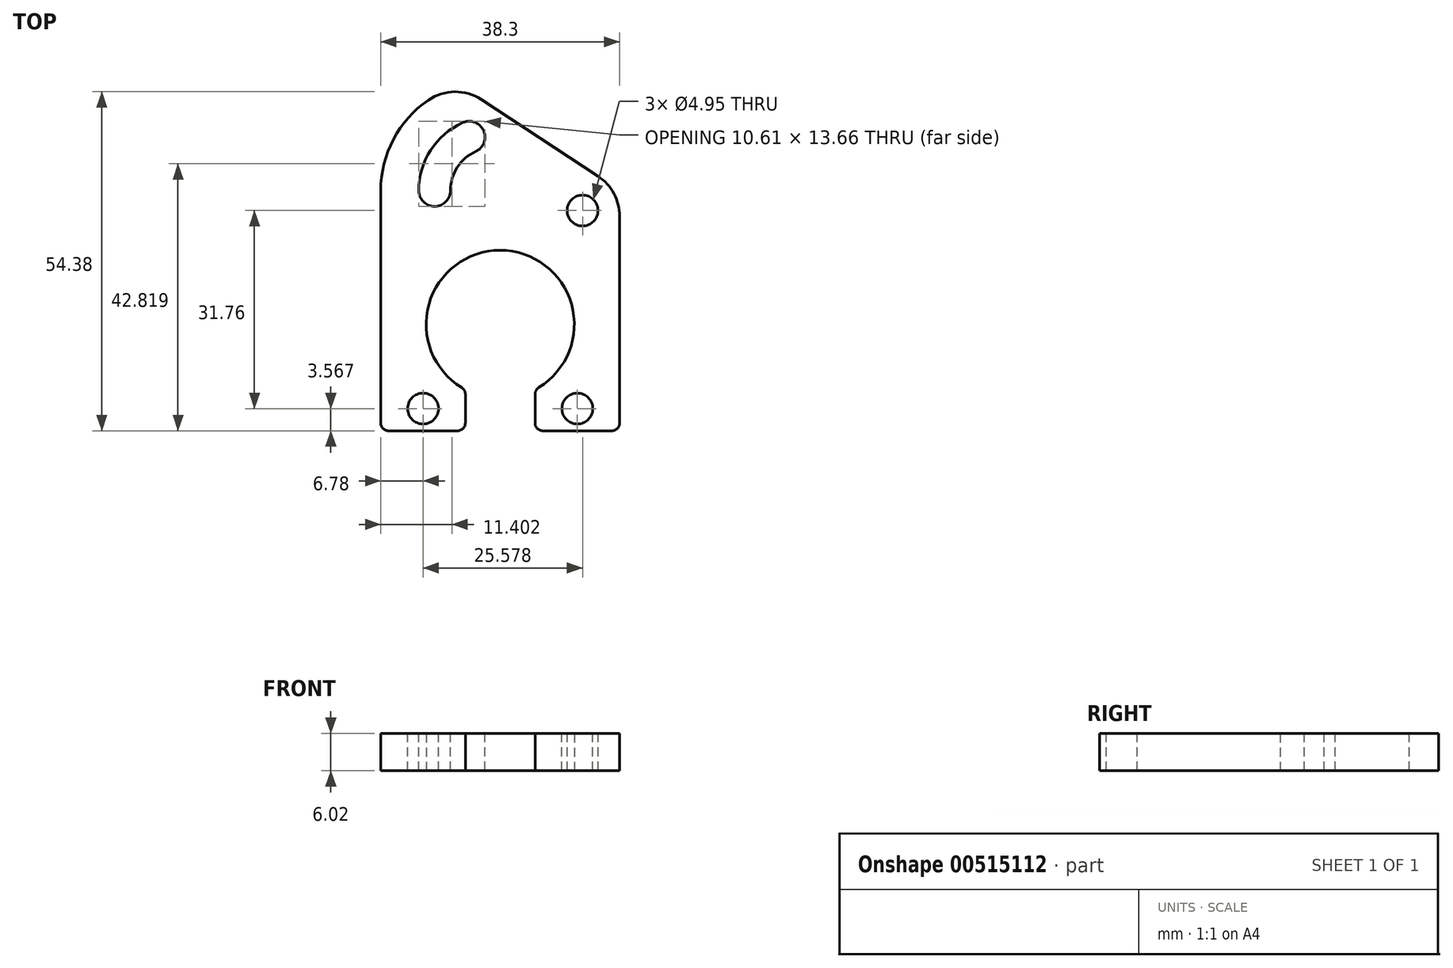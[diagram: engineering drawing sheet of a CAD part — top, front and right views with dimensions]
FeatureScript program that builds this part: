
annotation { "Feature Type Name" : "Feature", "Feature Type Description" : "" }
export const myFeature = defineFeature(function(context is Context, id is Id, definition is map)
    precondition{}
    {
        {
            var Q0;
            Q0=qCreatedBy(makeId("Top.planeOp"),FACE);
            var sketch = newSketch(context, id + "F0", { "sketchPlane" : qUnion([Q0])});
            skArc(sketch, "E0", {"start": v(5.59, -10.48) * mm, "mid": v(0, 11.87) * mm, "end": v(-5.59, -10.48) * mm});
            skLineSegment(sketch, "E1", {"start": v(19.15, -17.08) * mm, "end": v(19.15, 21.45) * mm});
            skLineSegment(sketch, "E2", {"start": v(19.15, 21.45) * mm, "end": v(-6.5, 38.34) * mm});
            skLineSegment(sketch, "E3", {"start": v(-19.15, -17.08) * mm, "end": v(-19.15, 21.45) * mm});
            skLineSegment(sketch, "E4", {"start": v(-19.15, -17.08) * mm, "end": v(-5.59, -17.08) * mm});
            skLineSegment(sketch, "E5", {"start": v(5.59, -17.08) * mm, "end": v(19.15, -17.08) * mm});
            skLineSegment(sketch, "E6", {"start": v(-5.59, -10.48) * mm, "end": v(-5.59, -17.08) * mm});
            skLineSegment(sketch, "E7", {"start": v(5.59, -10.48) * mm, "end": v(5.59, -17.08) * mm});
            skArc(sketch, "E8", {"start": v(-19.15, 21.45) * mm, "mid": v(-15.64, 32) * mm, "end": v(-6.5, 38.34) * mm});
            skSolve(sketch);
        }
        {
            var Q0;
            Q0=makeQuery(id+"F0.imprint","IMPRINT",FACE,{"disambiguationData":[TD([[makeQuery(id+"F0.imprint","IMPRINT",EDGE,{"derivedFrom":sQuery(id+"F0.wireOp",EDGE,"E0")}),-1.0]])]});
            extrude(context, id + "F1", {"entities" : qUnion([Q0]), "depth" : 6.02 * mm, "offsetDistance" : 25.4 * mm});
        }
        {
            var Q0;
            Q0=makeQuery(id+"F1.opExtrude","CAP_FACE",FACE,{"disambiguationData":[OSD([sQuery(id+"F0.wireOp",EDGE,"E0"),sQuery(id+"F0.wireOp",EDGE,"E1"),sQuery(id+"F0.wireOp",EDGE,"E2"),sQuery(id+"F0.wireOp",EDGE,"E3"),sQuery(id+"F0.wireOp",EDGE,"E4"),sQuery(id+"F0.wireOp",EDGE,"E5"),sQuery(id+"F0.wireOp",EDGE,"E6"),sQuery(id+"F0.wireOp",EDGE,"E7"),sQuery(id+"F0.wireOp",EDGE,"E8")])],"isStart":false});
            var sketch = newSketch(context, id + "F2", { "sketchPlane" : qUnion([Q0])});
            skArc(sketch, "E9", {"start": v(-13.06, 21.45) * mm, "mid": v(-10.52, 18.91) * mm, "end": v(-7.98, 21.45) * mm});
            skArc(sketch, "E10", {"start": v(-13.06, 21.45) * mm, "mid": v(-11.15, 27.93) * mm, "end": v(-6.03, 32.34) * mm});
            skArc(sketch, "E11", {"start": v(-7.98, 21.45) * mm, "mid": v(-6.88, 25.18) * mm, "end": v(-3.93, 27.71) * mm});
            skArc(sketch, "E12", {"start": v(-3.93, 27.71) * mm, "mid": v(-2.67, 31.08) * mm, "end": v(-6.03, 32.34) * mm});
            skSolve(sketch);
        }
        {
            var Q0;
            Q0=makeQuery(id+"F2.imprint","IMPRINT",FACE,{"disambiguationData":[TD([[makeQuery(id+"F2.imprint","IMPRINT",EDGE,{"derivedFrom":sQuery(id+"F2.wireOp",EDGE,"E9")}),1.0]])]});
            var Q1;
            Q1=makeQuery(id+"F1.opExtrude","CAP_FACE",FACE,{"disambiguationData":[OSD([sQuery(id+"F0.wireOp",EDGE,"E0"),sQuery(id+"F0.wireOp",EDGE,"E1"),sQuery(id+"F0.wireOp",EDGE,"E2"),sQuery(id+"F0.wireOp",EDGE,"E3"),sQuery(id+"F0.wireOp",EDGE,"E4"),sQuery(id+"F0.wireOp",EDGE,"E5"),sQuery(id+"F0.wireOp",EDGE,"E6"),sQuery(id+"F0.wireOp",EDGE,"E7"),sQuery(id+"F0.wireOp",EDGE,"E8")])],"isStart":true});
            extrude(context, id + "F3", {"entities" : qUnion([Q0]), "operationType" : NewBodyOperationType.REMOVE, "endBound" : BoundingType.UP_TO_SURFACE, "oppositeDirection" : true, "depth" : 25.4 * mm, "endBoundEntityFace" : qUnion([Q1]), "offsetDistance" : 25.4 * mm});
        }
        {
            var Q0;
            Q0=makeQuery(id+"F1.opExtrude","SWEPT_EDGE",EDGE,{"disambiguationData":[OSD([sQuery(id+"F0.wireOp",EDGE,"E2"),sQuery(id+"F0.wireOp",EDGE,"E8")])]});
            var Q1;
            Q1=makeQuery(id+"F1.opExtrude","SWEPT_EDGE",EDGE,{"disambiguationData":[OSD([sQuery(id+"F0.wireOp",EDGE,"E1"),sQuery(id+"F0.wireOp",EDGE,"E2")])]});
            fillet(context, id + "F4", {"entities" : qUnion([Q0, Q1]), "radius" : 7.62 * mm, "tangentPropagation" : true, "allowEdgeOverflow" : false});
        }
        {
            var Q0;
            Q0=makeQuery(id+"F1.opExtrude","SWEPT_EDGE",EDGE,{"disambiguationData":[OSD([sQuery(id+"F0.wireOp",EDGE,"E3"),sQuery(id+"F0.wireOp",EDGE,"E4")])]});
            var Q1;
            Q1=makeQuery(id+"F1.opExtrude","SWEPT_EDGE",EDGE,{"disambiguationData":[OSD([sQuery(id+"F0.wireOp",EDGE,"E4"),sQuery(id+"F0.wireOp",EDGE,"E6")])]});
            var Q2;
            Q2=makeQuery(id+"F1.opExtrude","SWEPT_EDGE",EDGE,{"disambiguationData":[OSD([sQuery(id+"F0.wireOp",EDGE,"E5"),sQuery(id+"F0.wireOp",EDGE,"E7")])]});
            var Q3;
            Q3=makeQuery(id+"F1.opExtrude","SWEPT_EDGE",EDGE,{"disambiguationData":[OSD([sQuery(id+"F0.wireOp",EDGE,"E1"),sQuery(id+"F0.wireOp",EDGE,"E5")])]});
            var Q4;
            Q4=makeQuery(id+"F1.opExtrude","SWEPT_EDGE",EDGE,{"disambiguationData":[OSD([sQuery(id+"F0.wireOp",EDGE,"E0"),sQuery(id+"F0.wireOp",EDGE,"E7")])]});
            var Q5;
            Q5=makeQuery(id+"F1.opExtrude","SWEPT_EDGE",EDGE,{"disambiguationData":[OSD([sQuery(id+"F0.wireOp",EDGE,"E0"),sQuery(id+"F0.wireOp",EDGE,"E6")])]});
            fillet(context, id + "F5", {"entities" : qUnion([Q0, Q1, Q2, Q3, Q4, Q5]), "radius" : 1.27 * mm, "tangentPropagation" : true, "allowEdgeOverflow" : false});
        }
        {
            var Q0;
            Q0=makeQuery(id+"F1.opExtrude","CAP_FACE",FACE,{"disambiguationData":[OSD([sQuery(id+"F0.wireOp",EDGE,"E0"),sQuery(id+"F0.wireOp",EDGE,"E1"),sQuery(id+"F0.wireOp",EDGE,"E2"),sQuery(id+"F0.wireOp",EDGE,"E3"),sQuery(id+"F0.wireOp",EDGE,"E4"),sQuery(id+"F0.wireOp",EDGE,"E5"),sQuery(id+"F0.wireOp",EDGE,"E6"),sQuery(id+"F0.wireOp",EDGE,"E7"),sQuery(id+"F0.wireOp",EDGE,"E8")])],"isStart":false});
            var sketch = newSketch(context, id + "F6", { "sketchPlane" : qUnion([Q0])});
            skPoint(sketch, "E13.0", {"position": v(18.24, 20.96) * mm});
            skArc(sketch, "E14.0", {"start": v(19.15, 17.34) * mm, "mid": v(18.24, 20.96) * mm, "end": v(15.72, 23.7) * mm, "construction": true});
            skLineSegment(sketch, "E15", {"start": v(11.53, 17.34) * mm, "end": v(14.89, 19.15) * mm, "construction": true});
            skPoint(sketch, "E16.end.orphan", {"position": v(15.85, 17.34) * mm});
            skCircle(sketch, "E17", {"center": v(13.2, 18.25) * mm, "radius": 2.48 * mm});
            skCircle(sketch, "E18", {"center": v(-12.37, -13.51) * mm, "radius": 2.48 * mm});
            skPoint(sketch, "E18.centerSnap0", {"position": v(-5.59, -13.51) * mm});
            skPoint(sketch, "E18.centerSnap1", {"position": v(-12.37, -17.08) * mm});
            skCircle(sketch, "E19", {"center": v(12.37, -13.51) * mm, "radius": 2.48 * mm});
            skPoint(sketch, "E19.centerSnap0", {"position": v(12.37, -17.08) * mm});
            skPoint(sketch, "E19.centerSnap1", {"position": v(5.59, -13.51) * mm});
            skSolve(sketch);
        }
        {
            var Q0;
            Q0=makeQuery(id+"F6.imprint","IMPRINT",FACE,{"disambiguationData":[TD([[makeQuery(id+"F6.imprint","IMPRINT",EDGE,{"derivedFrom":sQuery(id+"F6.wireOp",EDGE,"E17")}),1.0]])]});
            var Q1;
            Q1=makeQuery(id+"F6.imprint","IMPRINT",FACE,{"disambiguationData":[TD([[makeQuery(id+"F6.imprint","IMPRINT",EDGE,{"derivedFrom":sQuery(id+"F6.wireOp",EDGE,"E18")}),1.0]])]});
            var Q2;
            Q2=makeQuery(id+"F6.imprint","IMPRINT",FACE,{"disambiguationData":[TD([[makeQuery(id+"F6.imprint","IMPRINT",EDGE,{"derivedFrom":sQuery(id+"F6.wireOp",EDGE,"E19")}),1.0]])]});
            var Q3;
            Q3=makeQuery(id+"F1.opExtrude","CAP_FACE",FACE,{"disambiguationData":[OSD([sQuery(id+"F0.wireOp",EDGE,"E0"),sQuery(id+"F0.wireOp",EDGE,"E1"),sQuery(id+"F0.wireOp",EDGE,"E2"),sQuery(id+"F0.wireOp",EDGE,"E3"),sQuery(id+"F0.wireOp",EDGE,"E4"),sQuery(id+"F0.wireOp",EDGE,"E5"),sQuery(id+"F0.wireOp",EDGE,"E6"),sQuery(id+"F0.wireOp",EDGE,"E7"),sQuery(id+"F0.wireOp",EDGE,"E8")])],"isStart":true});
            extrude(context, id + "F7", {"entities" : qUnion([Q0, Q1, Q2]), "operationType" : NewBodyOperationType.REMOVE, "endBound" : BoundingType.UP_TO_SURFACE, "oppositeDirection" : true, "depth" : 25.4 * mm, "endBoundEntityFace" : qUnion([Q3]), "offsetDistance" : 25.4 * mm});
        }
    });
